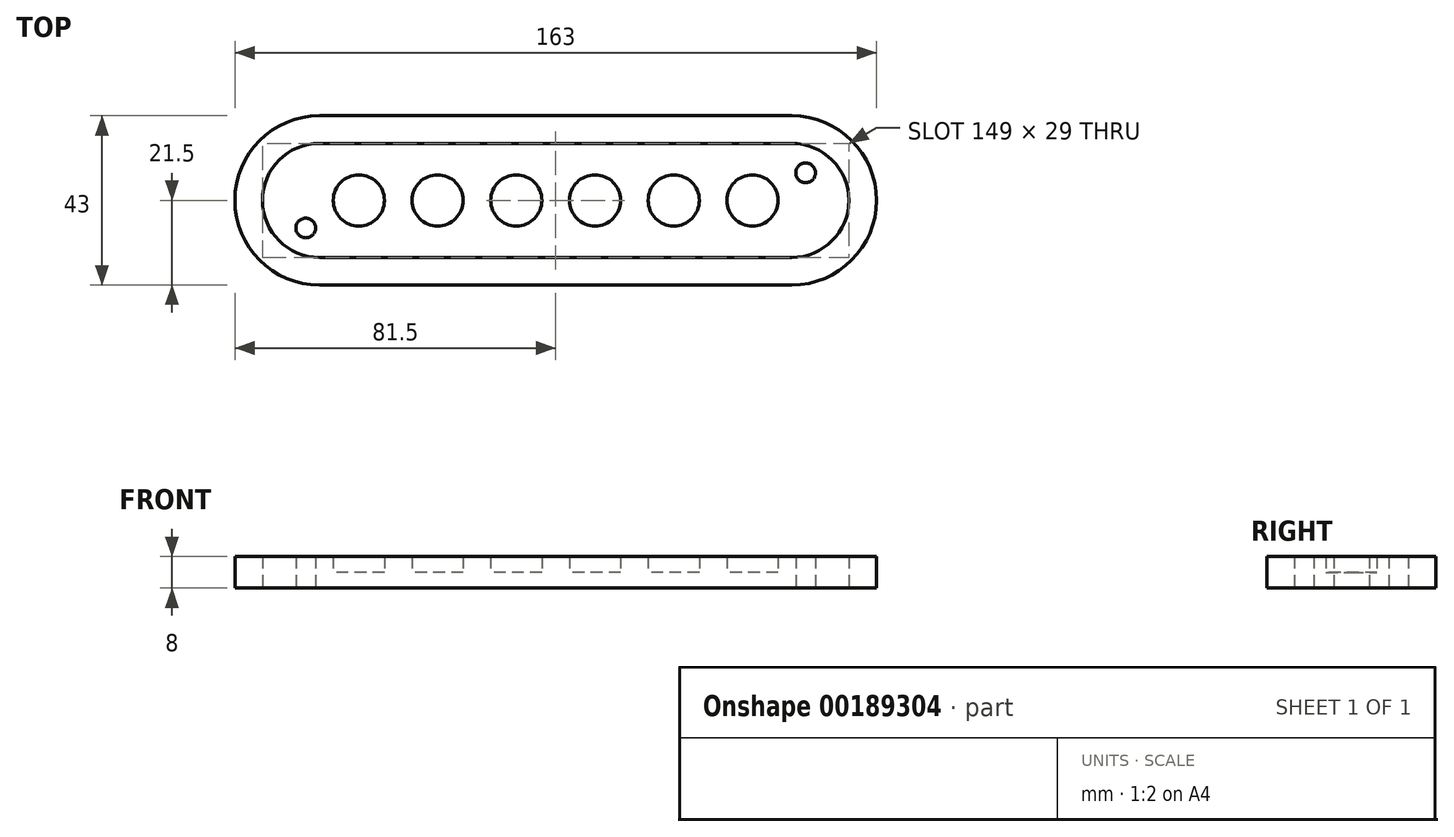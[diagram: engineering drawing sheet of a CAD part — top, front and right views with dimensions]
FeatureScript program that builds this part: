
annotation { "Feature Type Name" : "Feature", "Feature Type Description" : "" }
export const myFeature = defineFeature(function(context is Context, id is Id, definition is map)
    precondition{}
    {
        {
            var Q0;
            Q0=qCreatedBy(makeId("Top.planeOp"),FACE);
            var sketch = newSketch(context, id + "F0", { "sketchPlane" : qUnion([Q0])});
            skArc(sketch, "E0", {"start": v(0, 14.5) * mm, "mid": v(-14.5, 0) * mm, "end": v(0, -14.5) * mm});
            skArc(sketch, "E1", {"start": v(120, -14.5) * mm, "mid": v(134.5, 0) * mm, "end": v(120, 14.5) * mm});
            skLineSegment(sketch, "E2", {"start": v(0, 14.5) * mm, "end": v(120, 14.5) * mm});
            skLineSegment(sketch, "E3", {"start": v(120, -14.5) * mm, "end": v(0, -14.5) * mm});
            skCircle(sketch, "E4", {"center": v(10, 0) * mm, "radius": 6.5 * mm});
            skCircle(sketch, "E5.1.0.0", {"center": v(30, 0) * mm, "radius": 6.5 * mm});
            skCircle(sketch, "E5.2.0.0", {"center": v(50, 0) * mm, "radius": 6.5 * mm});
            skCircle(sketch, "E5.3.0.0", {"center": v(70, 0) * mm, "radius": 6.5 * mm});
            skCircle(sketch, "E5.4.0.0", {"center": v(90, 0) * mm, "radius": 6.5 * mm});
            skCircle(sketch, "E5.5.0.0", {"center": v(110, 0) * mm, "radius": 6.5 * mm});
            skLineSegment(sketch, "E5.direction1", {"start": v(10, 0) * mm, "end": v(30, 0) * mm, "construction": true});
            skLineSegment(sketch, "E6", {"start": v(110, 0) * mm, "end": v(120, 0) * mm, "construction": true});
            skLineSegment(sketch, "E7", {"start": v(10, 0) * mm, "end": v(0, 0) * mm, "construction": true});
            skLineSegment(sketch, "E8", {"start": v(60, 14.5) * mm, "end": v(60, -14.5) * mm, "construction": true});
            skCircle(sketch, "E9", {"center": v(-3.5, 7) * mm, "radius": 2.5 * mm});
            skCircle(sketch, "E10.MirrorC", {"center": v(-3.5, -7) * mm, "radius": 2.5 * mm});
            skCircle(sketch, "E11.MirrorC", {"center": v(123.5, -7) * mm, "radius": 2.5 * mm});
            skCircle(sketch, "E12.MirrorC", {"center": v(123.5, 7) * mm, "radius": 2.5 * mm});
            skLineSegment(sketch, "E13", {"start": v(0, 0) * mm, "end": v(0, 14.5) * mm, "construction": true});
            skSolve(sketch);
        }
        {
            var Q0;
            Q0=makeQuery(id+"F0.imprint","IMPRINT",FACE,{"disambiguationData":[TD([[makeQuery(id+"F0.imprint","IMPRINT",EDGE,{"derivedFrom":sQuery(id+"F0.wireOp",EDGE,"E0")}),1.0]])]});
            extrude(context, id + "F1", {"entities" : qUnion([Q0]), "depth" : 8 * mm});
        }
        {
            var Q0;
            Q0=qCreatedBy(makeId("Top.planeOp"),FACE);
            var sketch = newSketch(context, id + "F2", { "sketchPlane" : qUnion([Q0])});
            skLineSegment(sketch, "E14.0", {"start": v(0, 21.5) * mm, "end": v(120, 21.5) * mm});
            skArc(sketch, "E14.1", {"start": v(0, 21.5) * mm, "mid": v(-21.5, 0) * mm, "end": v(0, -21.5) * mm});
            skLineSegment(sketch, "E14.2", {"start": v(120, -21.5) * mm, "end": v(0, -21.5) * mm});
            skArc(sketch, "E14.3", {"start": v(120, -21.5) * mm, "mid": v(141.5, 0) * mm, "end": v(120, 21.5) * mm});
            skSolve(sketch);
        }
        {
            var Q0;
            Q0 = qSketchRegion(id + "F2", true);
            extrude(context, id + "F3", {"entities" : qUnion([Q0]), "depth" : 8 * mm});
        }
        {
            var Q0;
            Q0=makeQuery(id+"F0.imprint","IMPRINT",FACE,{"disambiguationData":[TD([[makeQuery(id+"F0.imprint","IMPRINT",EDGE,{"derivedFrom":sQuery(id+"F0.wireOp",EDGE,"E10.MirrorC")}),-1.0]])]});
            var Q1;
            Q1=makeQuery(id+"F0.imprint","IMPRINT",FACE,{"disambiguationData":[TD([[makeQuery(id+"F0.imprint","IMPRINT",EDGE,{"derivedFrom":sQuery(id+"F0.wireOp",EDGE,"E9")}),1.0]])]});
            var Q2;
            Q2=makeQuery(id+"F0.imprint","IMPRINT",FACE,{"disambiguationData":[TD([[makeQuery(id+"F0.imprint","IMPRINT",EDGE,{"derivedFrom":sQuery(id+"F0.wireOp",EDGE,"E12.MirrorC")}),-1.0]])]});
            var Q3;
            Q3=makeQuery(id+"F0.imprint","IMPRINT",FACE,{"disambiguationData":[TD([[makeQuery(id+"F0.imprint","IMPRINT",EDGE,{"derivedFrom":sQuery(id+"F0.wireOp",EDGE,"E11.MirrorC")}),1.0]])]});
            extrude(context, id + "F4", {"entities" : qUnion([Q0, Q1, Q2, Q3]), "operationType" : NewBodyOperationType.REMOVE, "endBound" : BoundingType.UP_TO_NEXT, "depth" : 25 * mm});
        }
        {
            var Q0;
            Q0=makeQuery(id+"F0.imprint","IMPRINT",FACE,{"disambiguationData":[TD([[makeQuery(id+"F0.imprint","IMPRINT",EDGE,{"derivedFrom":sQuery(id+"F0.wireOp",EDGE,"E4")}),1.0]])]});
            var Q1;
            Q1=makeQuery(id+"F0.imprint","IMPRINT",FACE,{"disambiguationData":[TD([[makeQuery(id+"F0.imprint","IMPRINT",EDGE,{"derivedFrom":sQuery(id+"F0.wireOp",EDGE,"E5.1.0.0")}),1.0]])]});
            var Q2;
            Q2=makeQuery(id+"F0.imprint","IMPRINT",FACE,{"disambiguationData":[TD([[makeQuery(id+"F0.imprint","IMPRINT",EDGE,{"derivedFrom":sQuery(id+"F0.wireOp",EDGE,"E5.2.0.0")}),1.0]])]});
            var Q3;
            Q3=makeQuery(id+"F0.imprint","IMPRINT",FACE,{"disambiguationData":[TD([[makeQuery(id+"F0.imprint","IMPRINT",EDGE,{"derivedFrom":sQuery(id+"F0.wireOp",EDGE,"E5.3.0.0")}),1.0]])]});
            var Q4;
            Q4=makeQuery(id+"F0.imprint","IMPRINT",FACE,{"disambiguationData":[TD([[makeQuery(id+"F0.imprint","IMPRINT",EDGE,{"derivedFrom":sQuery(id+"F0.wireOp",EDGE,"E5.4.0.0")}),1.0]])]});
            var Q5;
            Q5=makeQuery(id+"F0.imprint","IMPRINT",FACE,{"disambiguationData":[TD([[makeQuery(id+"F0.imprint","IMPRINT",EDGE,{"derivedFrom":sQuery(id+"F0.wireOp",EDGE,"E5.5.0.0")}),1.0]])]});
            extrude(context, id + "F5", {"entities" : qUnion([Q0, Q1, Q2, Q3, Q4, Q5]), "operationType" : NewBodyOperationType.REMOVE, "depth" : 4 * mm});
        }
    });
